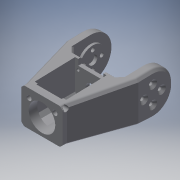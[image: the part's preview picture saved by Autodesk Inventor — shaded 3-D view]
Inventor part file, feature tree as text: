
AUTODESK INVENTOR PART (.ipt)
format: ipt  version: 2018 (Build 220112000, 112)  size: 1,037,824 bytes
history: native  units: mm
features: sketch x39, extrude x34, projected_geometry x33, hole x10, fillet x10, chamfer x10, mirror x1, plane x1
ambient origin geometry x8: Origin, YZ Plane, XZ Plane, XY Plane, X Axis, Y Axis, Z Axis, Center Point
bodies: Solid1 (feature_tree)
feature tree (138):
  extrude  "Extrusion1"  Depth=45.0mm
  extrude  "Extrusion2"  Depth=2.25mm
  hole  "Hole1"  [1 undecoded]
  hole  "Hole2"  [1 undecoded]
  fillet  "Fillet1"  Radius=14.0mm
  extrude  "Extrusion3"  Depth=18.5mm
  extrude  "Extrusion4"  Depth=10.0mm
  extrude  "Extrusion5"  Depth=2.195mm
  extrude  "Extrusion6"  Depth=20.5mm
  hole  "Hole3"  [1 undecoded]
  extrude  "Extrusion7"  Depth=0.5mm
  extrude  "Extrusion8"  Depth=5.0mm TaperAngle=0.0deg
  extrude  "Extrusion9"  Depth=10.0mm
  extrude  "Extrusion10"  Depth=10.0mm
  extrude  "Extrusion11"  Depth=14.5mm
  extrude  "Extrusion12"  Depth=14.5mm
  extrude  "Extrusion13"  Depth=5.0mm
  extrude  "Extrusion14"  Depth=2.25mm
  extrude  "Extrusion15"  Depth=5.0mm
  extrude  "Extrusion16"  Depth=9.0mm
  extrude  "Extrusion17"  Depth=4.0mm
  chamfer  "Chamfer1"  Distance=1.0mm
  fillet  "Fillet7"  Radius=20.7mm
  fillet  "Fillet8"  Radius=32.0mm
  mirror  "Mirror1"
  extrude  "Extrusion19"  Depth=1.0mm TaperAngle=0.0deg
  extrude  "Extrusion20"  Depth=8.0mm
  extrude  "Extrusion21"  Depth=0.2mm TaperAngle=0.0deg
  extrude  "Extrusion22"  Depth=0.5mm TaperAngle=0.0deg
  sketch  "Sketch29"  dims[d77=12.25mm d78=0.0mm d80=8.0mm]
  extrude  "Extrusion23"  Depth=5.0mm TaperAngle=0.0deg
  extrude  "Extrusion24"  Depth=0.2mm TaperAngle=0.0deg
  plane  "Work Plane1"
  extrude  "Extrusion25"  Depth=2.5mm TaperAngle=45.0deg
  extrude  "Extrusion26"  Depth=0.5mm
  extrude  "Extrusion27"  Depth=8.0mm
  extrude  "Extrusion28"  Depth=3.0mm TaperAngle=0.0deg
  extrude  "Extrusion29"  Depth=33.0mm
  extrude  "Extrusion30"  Depth=56.0mm
  extrude  "Extrusion31"  Depth=25.0mm TaperAngle=0.0deg
  chamfer  "Chamfer2"  Distance=6.0mm
  hole  "Hole6"  [1 undecoded]
  chamfer  "Chamfer3"  Distance=4.5mm
  extrude  "Extrusion32"  Depth=1.8mm TaperAngle=0.0deg
  extrude  "Extrusion33"  Depth=1.8mm
  chamfer  "Chamfer4"  Distance=12.0mm
  chamfer  "Chamfer5"  Distance=12.0mm
  chamfer  "Chamfer6"  Distance=40.0mm
  fillet  "Fillet9"  Radius=40.0mm
  extrude  "Extrusion34"  Depth=1.8mm
  chamfer  "Chamfer7"  Distance=1.8mm
  sketch  "Sketch42"  dims[d146=6.0mm d147=0.0mm d149=42.0mm]
  hole  "Hole7"  [1 undecoded]
  hole  "Hole8"  [1 undecoded]
  hole  "Hole9"  [1 undecoded]
  fillet  "Fillet10"  Radius=14.0mm
  chamfer  "Chamfer8"  Distance=1.2mm Angle=45.0deg
  chamfer  "Chamfer9"  Distance=7.0mm
  fillet  "Fillet11"  Radius=2.5mm
  fillet  "Fillet12"  Radius=7.0mm
  extrude  "Extrusion35"  Depth=1.8mm TaperAngle=0.0deg
  sketch  "Sketch45"  dims[d151=4.5mm d152=4.5mm d153=40.0mm d154=0.0mm d155=28.0mm d156=12.0mm d157=12.0mm d158=40.0mm d159=0.0mm d160=40.0mm d161=0.0mm d162=20.5mm d163=1.8mm d164=0.0mm d165=20.5mm d166=3.3mm d167=0.0mm d168=2.0mm d169=2.0mm d170=45.0deg d171=14.0mm d172=3.1mm d173=6.0mm d174=6.3mm d175=2.0mm d176=90.0deg d177=8.0mm d178=20.594885mm d179=1.2mm d180=2.0mm d181=45.0deg d182=7.0mm d183=2.5mm d184=0.0mm d185=7.0mm d186=2.5mm d187=0.0mm d188=3.0mm d189=15.0mm d190=45.0deg d191=3.0mm d192=15.0mm d193=45.0deg d194=3.0mm d195=15.0mm d196=45.0deg d197=2.0mm d198=12.0mm d199=2.0mm d200=15.0mm d201=20.0mm d202=0.0mm d203=2.0mm d204=15.0mm d205=45.0deg d206=2.9mm d207=2.9mm d208=3.18mm d209=3.18mm d210=4.0mm d211=6.0mm d212=6.3mm d213=2.0mm d214=90.0deg d215=8.0mm d216=20.594885mm d217=1.567mm d218=25.0mm d219=6.3mm d220=2.0mm d221=90.0deg d222=25.0mm d223=20.594885mm d224=2.15mm d225=20.0mm d226=4.4mm d227=2.0mm d228=90.0deg d229=10.0mm d230=0.0mm d231=0.5mm d232=2.0mm d233=15.0mm d234=45.0deg d235=2.0mm d236=15.0mm d237=45.0deg d238=1.0mm d239=3.0mm d240=3.9mm d241=3.9mm d242=3.5mm d243=0.0mm d244=2.75mm d245=2.75mm d246=2.5mm d247=1.567mm d248=4.0mm d249=4.4mm d250=2.0mm d251=90.0deg d252=40.0mm d253=20.594885mm d254=2.1mm d255=4.0mm d256=4.4mm d257=2.0mm d258=90.0deg d259=28.25mm d260=0.0mm d261=3.9mm d262=4.0mm d263=4.4mm d264=2.0mm d265=90.0deg d266=20.0mm d267=0.0mm d268=0.2mm d269=2.0mm d270=2.0mm d271=1.8mm d272=15.0mm d273=45.0deg]
  hole  "Hole10"  [1 undecoded]
  hole  "Hole11"  [1 undecoded]
  hole  "Hole12"  [1 undecoded]
  fillet  "Fillet13"  Radius=2.0mm
  fillet  "Fillet14"  Radius=12.0mm
  fillet  "Fillet15"  Radius=2.0mm
  chamfer  "Chamfer10"  Distance=15.0mm
  sketch  "Sketch1"  dims[d0=24.5mm d1=45.0mm]
  sketch  "Sketch2"  dims[d2=1.95mm d3=0.0mm d4=2.25mm]
  projected_geometry  "Projected Loop1"
  sketch  "Sketch3"  dims[d5=20.0mm d6=2.25mm]
  projected_geometry  "Projected Loop2"
  sketch  "Sketch4"  dims[d7=5.25mm d8=5.25mm d9=14.0mm]
  projected_geometry  "Projected Loop3"
  sketch  "Sketch5"  dims[d10=5.25mm d11=18.5mm]
  projected_geometry  "Projected Loop4"
  sketch  "Sketch6"  dims[d12=10.0mm d13=0.0mm d14=20.5mm]
  projected_geometry  "Projected Loop5"
  sketch  "Sketch7"  dims[d15=2.0mm d16=2.195mm]
  projected_geometry  "Projected Loop6"
  sketch  "Sketch8"  dims[d17=2.0mm]
  projected_geometry  "Projected Loop7"
  sketch  "Sketch9"  dims[d18=2.4mm d19=6.0mm d20=4.4mm d21=2.0mm d22=90.0deg d23=8.0mm d24=20.594885mm d25=20.5mm]
  projected_geometry  "Projected Loop8"
  projected_geometry  "Projected Loop9"
  sketch  "Sketch10"  dims[d26=26.65mm d27=2.0mm]
  projected_geometry  "Projected Loop10"
  projected_geometry  "Projected Loop11"
  sketch  "Sketch11"  dims[d28=2.0mm]
  projected_geometry  "Projected Loop12"
  sketch  "Sketch12"  dims[d29=2.4mm d30=6.0mm d31=4.4mm d32=2.0mm d33=90.0deg d34=8.0mm d35=20.594885mm d36=0.5mm]
  sketch  "Sketch13"  dims[d37=18.0mm d38=5.0mm d39=0.0mm]
  sketch  "Sketch14"  dims[d41=10.0mm d42=0.0mm d43=24.5mm]
  projected_geometry  "Projected Loop13"
  sketch  "Sketch15"  dims[d44=1.15mm d45=0.0mm d46=10.0mm]
  sketch  "Sketch16"  dims[d47=21.0mm d48=14.5mm]
  projected_geometry  "Projected Loop14"
  sketch  "Sketch17"  dims[d49=20.0mm d50=14.5mm]
  projected_geometry  "Projected Loop15"
  sketch  "Sketch18"  dims[d51=24.5mm d52=5.0mm]
  projected_geometry  "Projected Loop16"
  sketch  "Sketch19"  dims[d53=5.0mm d54=2.25mm]
  projected_geometry  "Projected Loop17"
  sketch  "Sketch20"  dims[d55=2.25mm d56=5.0mm]
  projected_geometry  "Projected Loop18"
  sketch  "Sketch25"  dims[d57=5.0mm d58=9.0mm]
  projected_geometry  "Projected Loop22"
  sketch  "Sketch26"  dims[d59=14.75mm d60=4.0mm d61=1.0mm d62=0.0mm d63=20.7mm]
  sketch  "Sketch27"  dims[d64=2.4mm d65=6.0mm d66=4.4mm d67=2.0mm d68=90.0deg d69=8.0mm d70=20.594885mm d72=32.0mm]
  projected_geometry  "Projected Loop23"
  sketch  "Sketch28"  dims[d73=5.0mm d74=0.0mm d75=1.0mm d76=0.0mm]
  projected_geometry  "Projected Loop24"
  sketch  "Sketch31"  dims[d81=4.5mm d82=0.0mm d84=0.2mm d85=0.0mm]
  projected_geometry  "Projected Loop25"
  sketch  "Sketch32"  dims[d86=21.0mm d87=0.5mm d88=0.0mm]
  projected_geometry  "Projected Loop26"
  sketch  "Sketch33"  dims[d91=8.0mm d92=0.0mm d93=5.0mm d94=0.0mm]
  sketch  "Sketch34"  dims[d95=5.0mm d96=0.0mm d98=0.2mm d99=0.0mm]
  sketch  "Sketch35"  dims[d100=0.2mm d101=0.0mm d102=2.5mm d103=2.0mm d104=45.0deg]
  projected_geometry  "Projected Loop27"
  sketch  "Sketch36"  dims[d105=1.5mm d114=0.5mm]
  sketch  "Sketch37"  dims[d128=4.0mm d129=0.0mm d130=8.0mm]
  sketch  "Sketch38"  dims[d131=3.0mm d132=0.0mm d133=3.0mm d134=0.0mm]
  projected_geometry  "Projected Loop28"
  sketch  "Sketch39"  dims[d135=25.0mm d136=0.0mm d137=33.0mm]
  projected_geometry  "Projected Loop29"
  sketch  "Sketch40"  dims[d138=2.5mm d139=56.0mm]
  projected_geometry  "Projected Loop30"
  sketch  "Sketch41"  dims[d140=25.0mm d141=0.0mm d142=25.0mm d143=0.0mm d144=6.0mm d145=0.0mm]
  sketch  "Sketch44"  dims[d150=4.5mm]
  projected_geometry  "Projected Loop31"
  projected_geometry  "Projected Loop32"
  projected_geometry  "Projected Loop33"
  projected_geometry  "Project Cut Edges1"
  projected_geometry  "Project Cut Edges2"
  projected_geometry  "Project Cut Edges3"
note: 10 required parameter values undecoded (feature->parameter linkage not recoverable at this tier; creation-order binding heuristic only, values carry confidence <= 0.55)
